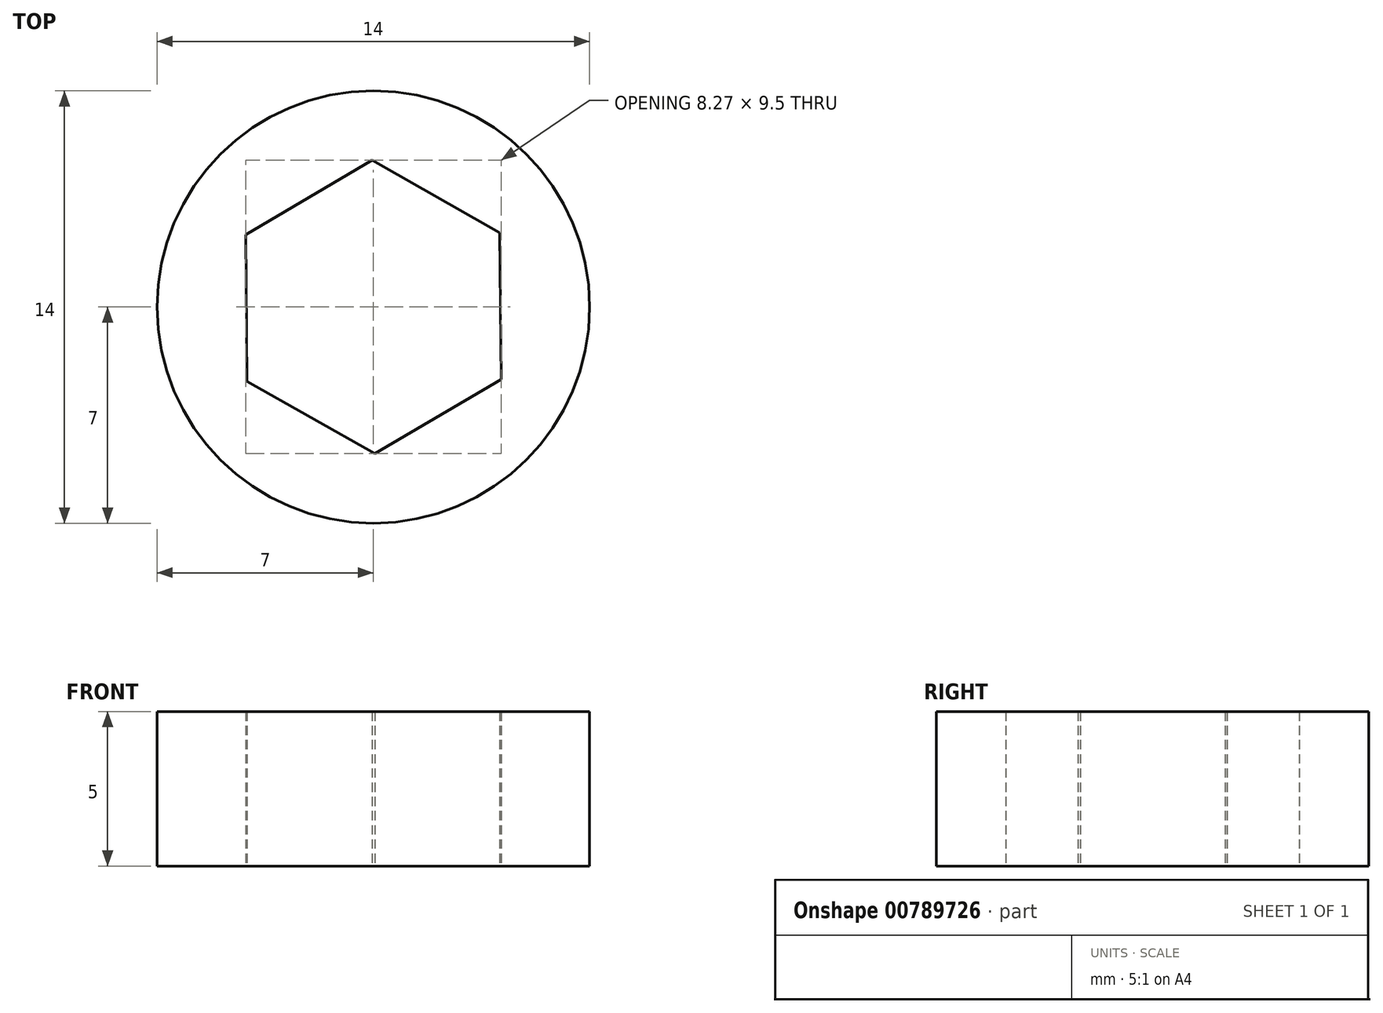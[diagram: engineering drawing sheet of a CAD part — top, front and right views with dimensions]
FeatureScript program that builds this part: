
annotation { "Feature Type Name" : "Feature", "Feature Type Description" : "" }
export const myFeature = defineFeature(function(context is Context, id is Id, definition is map)
    precondition{}
    {
        {
            var Q0;
            Q0=qCreatedBy(makeId("Top.planeOp"),FACE);
            var sketch = newSketch(context, id + "F0", { "sketchPlane" : qUnion([Q0])});
            skCircle(sketch, "E0.cCircle", {"center": v(-20, 0) * mm, "radius": 4.75 * mm, "construction": true});
            skLineSegment(sketch, "E0.0", {"start": v(-24.1, -2.41) * mm, "end": v(-24.13, 2.34) * mm});
            skLineSegment(sketch, "E0.1", {"start": v(-24.13, 2.34) * mm, "end": v(-20.04, 4.75) * mm});
            skLineSegment(sketch, "E0.2", {"start": v(-20.04, 4.75) * mm, "end": v(-15.9, 2.41) * mm});
            skLineSegment(sketch, "E0.3", {"start": v(-15.9, 2.41) * mm, "end": v(-15.87, -2.34) * mm});
            skLineSegment(sketch, "E0.4", {"start": v(-15.87, -2.34) * mm, "end": v(-19.96, -4.75) * mm});
            skLineSegment(sketch, "E0.5", {"start": v(-19.96, -4.75) * mm, "end": v(-24.1, -2.41) * mm});
            skCircle(sketch, "E1", {"center": v(-20, 0) * mm, "radius": 7 * mm});
            skSolve(sketch);
        }
        {
            var Q0;
            Q0=makeQuery(id+"F0.imprint","IMPRINT",FACE,{"disambiguationData":[TD([[makeQuery(id+"F0.imprint","IMPRINT",EDGE,{"derivedFrom":sQuery(id+"F0.wireOp",EDGE,"E0.0")}),1.0]])]});
            extrude(context, id + "F1", {"entities" : qUnion([Q0]), "depth" : 5 * mm, "offsetDistance" : 25 * mm});
        }
    });
